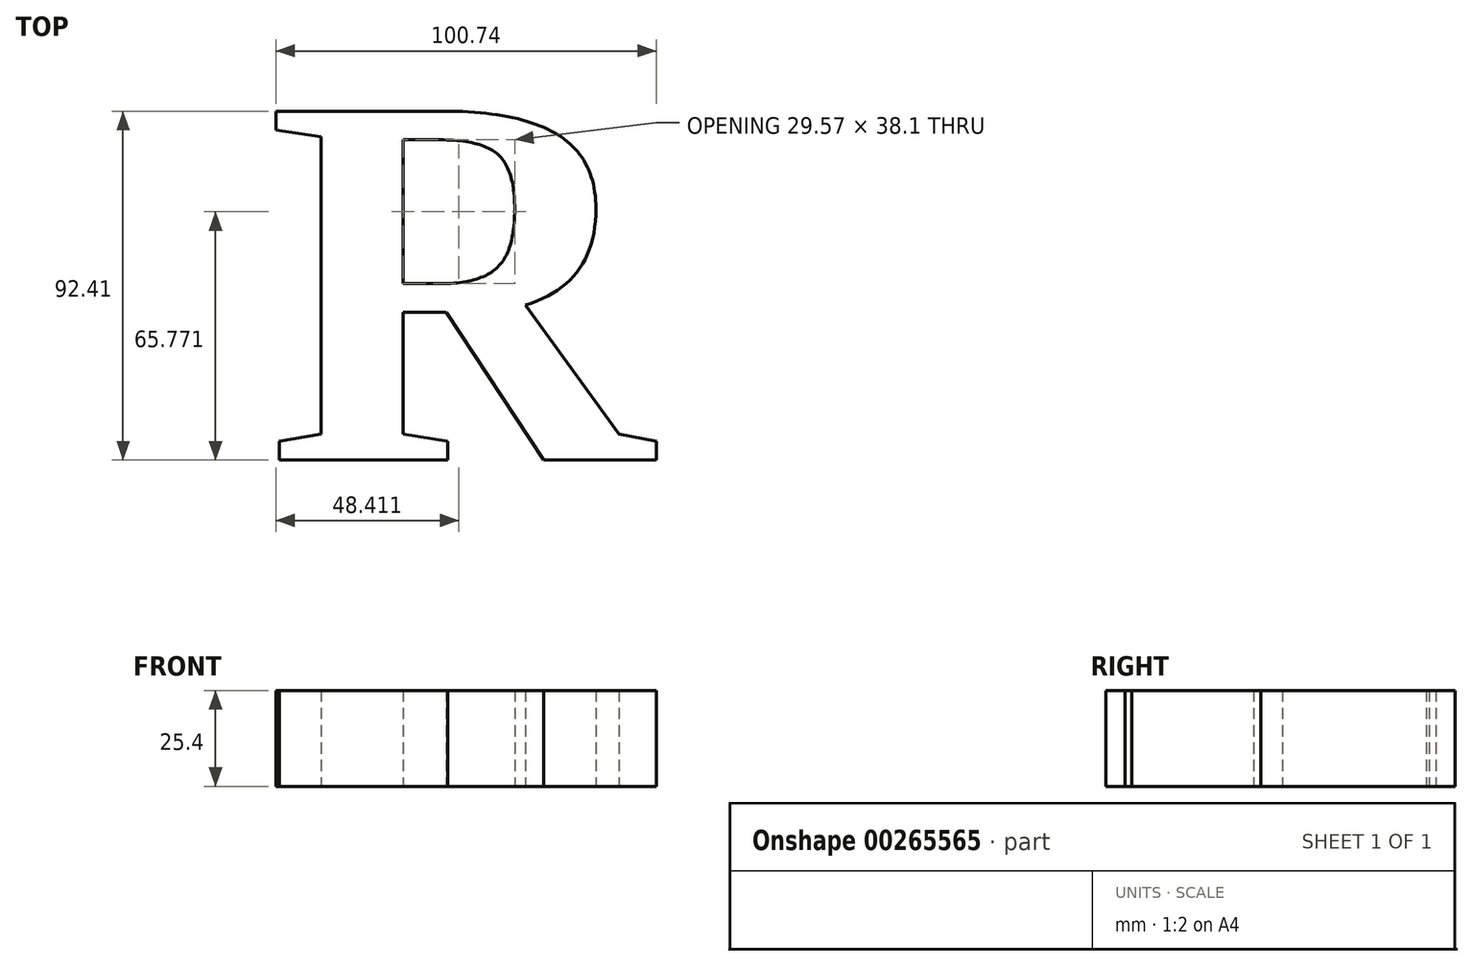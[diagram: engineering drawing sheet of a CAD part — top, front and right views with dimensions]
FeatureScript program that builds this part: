
annotation { "Feature Type Name" : "Feature", "Feature Type Description" : "" }
export const myFeature = defineFeature(function(context is Context, id is Id, definition is map)
    precondition{}
    {
        {
            var Q0;
            Q0=qCreatedBy(makeId("Top.planeOp"),FACE);
            var sketch = newSketch(context, id + "F0", { "sketchPlane" : qUnion([Q0])});
            skText(sketch, "E0", { "text": "R", "fontName": "Tinos-Bold.ttf"});
            const initialGuessF0  = {"E0": [-0.02766, -0.06821, 1, 0, 0.1016]};
            skSetInitialGuess(sketch, initialGuessF0);
            skSolve(sketch);
        }
        {
            var Q0;
            Q0=makeQuery(id+"F0.imprint","IMPRINT",FACE,{"disambiguationData":[TD([[makeQuery(id+"F0.imprint","IMPRINT",EDGE,{"derivedFrom":sQuery(id+"F0.wireOp",EDGE,"E0.sketch_text.stroke-0")}),-1.0]])]});
            extrude(context, id + "F1", {"entities" : qUnion([Q0]), "depth" : 25.4 * mm});
        }
    });
